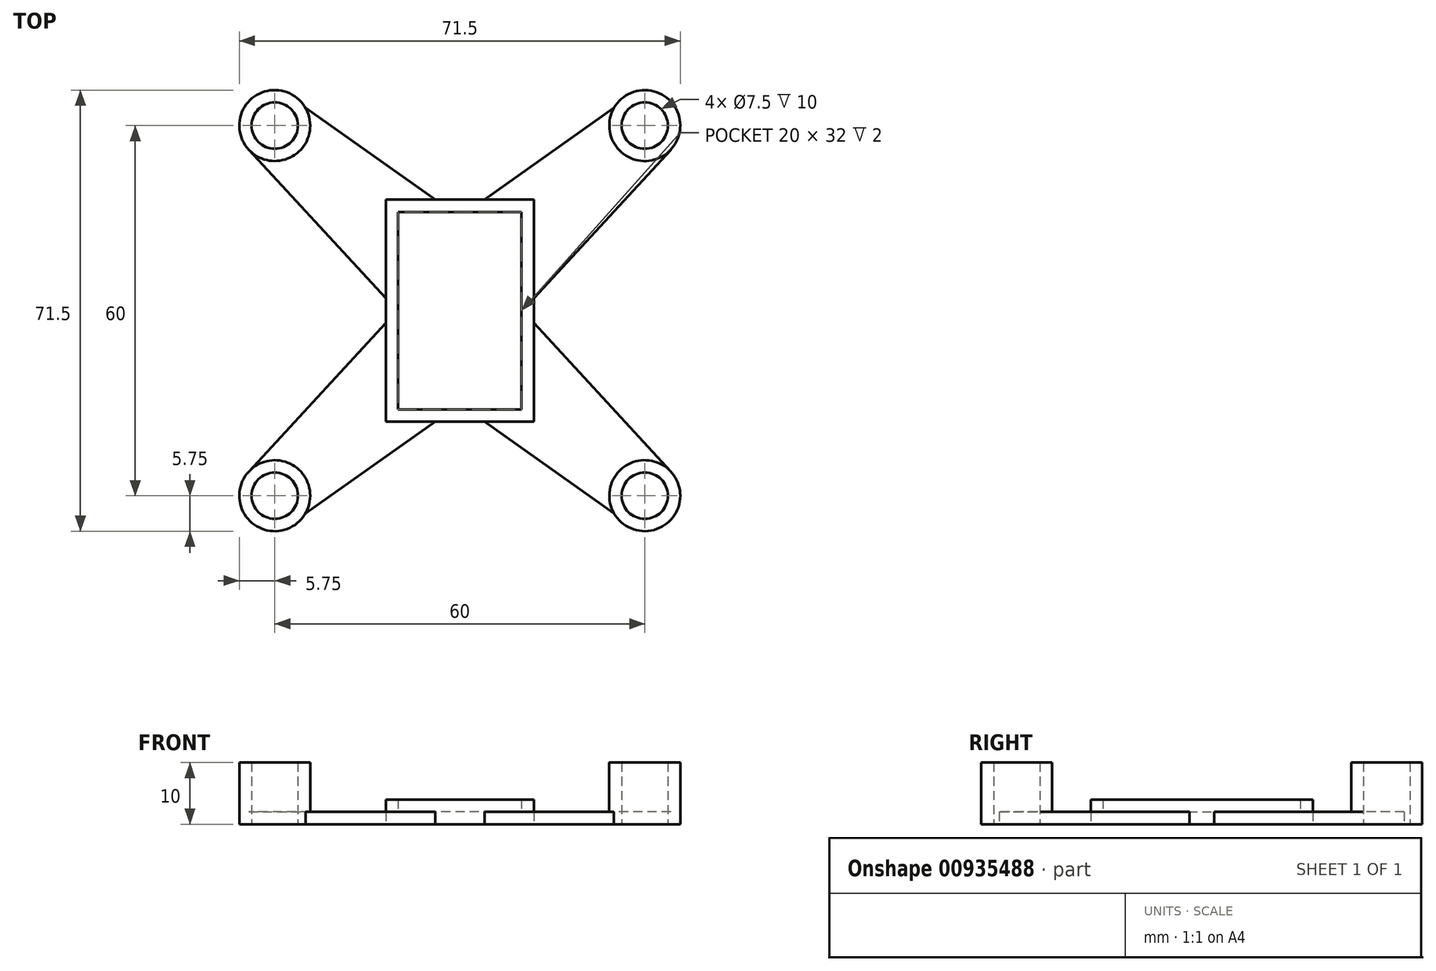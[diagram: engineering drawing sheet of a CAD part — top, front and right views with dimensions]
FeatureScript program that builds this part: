
annotation { "Feature Type Name" : "Feature", "Feature Type Description" : "" }
export const myFeature = defineFeature(function(context is Context, id is Id, definition is map)
    precondition{}
    {
        {
            var Q0;
            Q0=qCreatedBy(makeId("Top.planeOp"),FACE);
            var sketch = newSketch(context, id + "F0", { "sketchPlane" : qUnion([Q0])});
            skLineSegment(sketch, "E0.bottom", {"start": v(30, 30) * mm, "end": v(-30, 30) * mm, "construction": true});
            skLineSegment(sketch, "E0.top", {"start": v(30, -30) * mm, "end": v(-30, -30) * mm, "construction": true});
            skLineSegment(sketch, "E0.left", {"start": v(30, 30) * mm, "end": v(30, -30) * mm, "construction": true});
            skLineSegment(sketch, "E0.right", {"start": v(-30, 30) * mm, "end": v(-30, -30) * mm, "construction": true});
            skPoint(sketch, "E0.middle", {"position": v(0, 0) * mm});
            skCircle(sketch, "E1", {"center": v(-30, 30) * mm, "radius": 3.75 * mm});
            skCircle(sketch, "E2", {"center": v(30, 30) * mm, "radius": 3.75 * mm});
            skCircle(sketch, "E3", {"center": v(30, -30) * mm, "radius": 3.75 * mm});
            skCircle(sketch, "E4", {"center": v(-30, -30) * mm, "radius": 3.75 * mm});
            skCircle(sketch, "E5", {"center": v(30, 30) * mm, "radius": 5.75 * mm});
            skCircle(sketch, "E6", {"center": v(-30, -30) * mm, "radius": 5.75 * mm});
            skCircle(sketch, "E7", {"center": v(30, -30) * mm, "radius": 5.75 * mm});
            skCircle(sketch, "E8", {"center": v(-30, 30) * mm, "radius": 5.75 * mm});
            skLineSegment(sketch, "E9.bottom", {"start": v(-10, 16) * mm, "end": v(10, 16) * mm});
            skLineSegment(sketch, "E9.top", {"start": v(-10, -16) * mm, "end": v(10, -16) * mm});
            skLineSegment(sketch, "E9.left", {"start": v(-10, 16) * mm, "end": v(-10, -16) * mm});
            skLineSegment(sketch, "E9.right", {"start": v(10, 16) * mm, "end": v(10, -16) * mm});
            skLineSegment(sketch, "E10.bottom", {"start": v(-12, 18) * mm, "end": v(12, 18) * mm});
            skLineSegment(sketch, "E10.top", {"start": v(-12, -18) * mm, "end": v(12, -18) * mm});
            skLineSegment(sketch, "E10.left", {"start": v(-12, 18) * mm, "end": v(-12, -18) * mm});
            skLineSegment(sketch, "E10.right", {"start": v(12, 18) * mm, "end": v(12, -18) * mm});
            skLineSegment(sketch, "E11", {"start": v(-25, 32.84) * mm, "end": v(-4, 18) * mm});
            skLineSegment(sketch, "E12", {"start": v(-34.23, 26.1) * mm, "end": v(-12, 2) * mm});
            skLineSegment(sketch, "E13.MirrorCS", {"start": v(34.23, 26.1) * mm, "end": v(12, 2) * mm});
            skLineSegment(sketch, "E14.MirrorCS", {"start": v(25, 32.84) * mm, "end": v(4, 18) * mm});
            skLineSegment(sketch, "E15.MirrorCS", {"start": v(34.23, -26.1) * mm, "end": v(12, -2) * mm});
            skLineSegment(sketch, "E16.MirrorCS", {"start": v(25, -32.84) * mm, "end": v(4, -18) * mm});
            skLineSegment(sketch, "E17.MirrorCS", {"start": v(-25, -32.84) * mm, "end": v(-4, -18) * mm});
            skLineSegment(sketch, "E18.MirrorCS", {"start": v(-34.23, -26.1) * mm, "end": v(-12, -2) * mm});
            skSolve(sketch);
        }
        {
            var Q0;
            {var subQ0=sQuery(id+"F0.wireOp",EDGE,"E11");Q0=makeQuery(id+"F0.imprint","IMPRINT",FACE,{"disambiguationData":[TD([[makeQuery(id+"F0.imprint","IMPRINT",EDGE,{"derivedFrom":subQ0}),-1.0]])]});}
            var Q1;
            {var subQ0=sQuery(id+"F0.wireOp",EDGE,"E14.MirrorCS");Q1=makeQuery(id+"F0.imprint","IMPRINT",FACE,{"disambiguationData":[TD([[makeQuery(id+"F0.imprint","IMPRINT",EDGE,{"derivedFrom":subQ0}),1.0]])]});}
            var Q2;
            Q2=makeQuery(id+"F0.imprint","IMPRINT",FACE,{"disambiguationData":[TD([[makeQuery(id+"F0.imprint","IMPRINT",EDGE,{"derivedFrom":sQuery(id+"F0.wireOp",EDGE,"E9.bottom")}),-1.0]])]});
            var Q3;
            Q3=makeQuery(id+"F0.imprint","IMPRINT",FACE,{"disambiguationData":[TD([[makeQuery(id+"F0.imprint","IMPRINT",EDGE,{"derivedFrom":sQuery(id+"F0.wireOp",EDGE,"E9.bottom")}),1.0]])]});
            var Q4;
            Q4=makeQuery(id+"F0.imprint","IMPRINT",FACE,{"disambiguationData":[TD([[makeQuery(id+"F0.imprint","IMPRINT",EDGE,{"derivedFrom":sQuery(id+"F0.wireOp",EDGE,"E1")}),-1.0]])]});
            var Q5;
            {var subQ0=sQuery(id+"F0.wireOp",EDGE,"E17.MirrorCS");Q5=makeQuery(id+"F0.imprint","IMPRINT",FACE,{"disambiguationData":[TD([[makeQuery(id+"F0.imprint","IMPRINT",EDGE,{"derivedFrom":subQ0}),1.0]])]});}
            var Q6;
            {var subQ0=sQuery(id+"F0.wireOp",EDGE,"E15.MirrorCS");Q6=makeQuery(id+"F0.imprint","IMPRINT",FACE,{"disambiguationData":[TD([[makeQuery(id+"F0.imprint","IMPRINT",EDGE,{"derivedFrom":subQ0}),1.0]])]});}
            var Q7;
            Q7=makeQuery(id+"F0.imprint","IMPRINT",FACE,{"disambiguationData":[TD([[makeQuery(id+"F0.imprint","IMPRINT",EDGE,{"derivedFrom":sQuery(id+"F0.wireOp",EDGE,"E3")}),-1.0]])]});
            var Q8;
            Q8=makeQuery(id+"F0.imprint","IMPRINT",FACE,{"disambiguationData":[TD([[makeQuery(id+"F0.imprint","IMPRINT",EDGE,{"derivedFrom":sQuery(id+"F0.wireOp",EDGE,"E2")}),-1.0]])]});
            var Q9;
            Q9=makeQuery(id+"F0.imprint","IMPRINT",FACE,{"disambiguationData":[TD([[makeQuery(id+"F0.imprint","IMPRINT",EDGE,{"derivedFrom":sQuery(id+"F0.wireOp",EDGE,"E4")}),-1.0]])]});
            extrude(context, id + "F1", {"entities" : qUnion([Q0, Q1, Q2, Q3, Q4, Q5, Q6, Q7, Q8, Q9]), "depth" : 2 * mm, "offsetDistance" : 25 * mm});
        }
        {
            var Q0;
            Q0=makeQuery(id+"F0.imprint","IMPRINT",FACE,{"disambiguationData":[TD([[makeQuery(id+"F0.imprint","IMPRINT",EDGE,{"derivedFrom":sQuery(id+"F0.wireOp",EDGE,"E4")}),-1.0]])]});
            var Q1;
            Q1=makeQuery(id+"F0.imprint","IMPRINT",FACE,{"disambiguationData":[TD([[makeQuery(id+"F0.imprint","IMPRINT",EDGE,{"derivedFrom":sQuery(id+"F0.wireOp",EDGE,"E3")}),-1.0]])]});
            var Q2;
            Q2=makeQuery(id+"F0.imprint","IMPRINT",FACE,{"disambiguationData":[TD([[makeQuery(id+"F0.imprint","IMPRINT",EDGE,{"derivedFrom":sQuery(id+"F0.wireOp",EDGE,"E2")}),-1.0]])]});
            var Q3;
            Q3=makeQuery(id+"F0.imprint","IMPRINT",FACE,{"disambiguationData":[TD([[makeQuery(id+"F0.imprint","IMPRINT",EDGE,{"derivedFrom":sQuery(id+"F0.wireOp",EDGE,"E1")}),-1.0]])]});
            extrude(context, id + "F2", {"entities" : qUnion([Q0, Q1, Q2, Q3]), "operationType" : NewBodyOperationType.ADD, "depth" : 10 * mm, "offsetDistance" : 25 * mm});
        }
        {
            var Q0;
            Q0=qCreatedBy(makeId("Top.planeOp"),FACE);
            var sketch = newSketch(context, id + "F3", { "sketchPlane" : qUnion([Q0])});
            skSolve(sketch);
        }
        {
            var Q0;
            Q0 = qSketchRegion(id + "F3", true);
            var Q1;
            Q1=makeQuery(id+"F0.imprint","IMPRINT",FACE,{"disambiguationData":[TD([[makeQuery(id+"F0.imprint","IMPRINT",EDGE,{"derivedFrom":sQuery(id+"F0.wireOp",EDGE,"E9.bottom")}),1.0]])]});
            extrude(context, id + "F4", {"entities" : qUnion([Q0, Q1]), "operationType" : NewBodyOperationType.ADD, "depth" : 4 * mm, "offsetDistance" : 25 * mm});
        }
    });
